# Revit family: Kingsway Stable DA Doorset - S_Flush
name_source: partatom
category: Doors
revit_build: Autodesk Revit 2016 (Build: 20150701_1515(x64)
units: mm (PartAtom-declared; Revit-internal decimal feet)

## family parameters
Always vertical = Yes
Cut with Voids When Loaded = No
Host = Wall
OmniClass Number = 23.30.10.00
OmniClass Title = Doors
Room Calculation Point = No
Shared = No

## types (1)
- 1000 x 2100
    Action = Double (Anti-Barricade)
    Analytic Construction = <None>
    Architrave Finish = <By Category>
    Architrave Material = Solid hardwood.
    Bead Material = None.
    Configuration = Single Leaf (Stable)
    Description = The twin leaf, stable split door double action for clinics or servery areas.
    Door - Leaf Finish Notes = Classic Veneer – 'Oak', 'Ash', or 'Beech'
Classic Laminate – 'Formica Door Collection Matte58 Woods', or 'Formica Collection Colors'
Signature - 'Malmo (Egger H877 ST86 Light Lakeland Acacia)', 'Manhattan (Egger H1734 ST9 Intarsie Walnut Horizontal)', or 'Mayfair (Egger H853 ST86 Lava Grey Fleetwood Horizontal)'
    Door Leaf Height = 2054 mm  [stored 6.73885 ft]
    Door Leaf Width = 849 mm  [stored 2.78543 ft]
    DoorLeafHeightLower = 1000 mm  [stored 3.28084 ft]
    DoorLeafHeightUpper = 1051 mm
    Durability = Severe Duty Mechanical Strength (DD171).
    Error = No
    Fire Rating = NFR / FD30S
    Frame Finish = <By Category>
    Frame Thickness = 32 mm  [stored 0.104987 ft]
    Frame Thickness Leading Edge = 44 mm  [stored 0.144357 ft]
    Function = Interior
    Hardware - Blanking Plate = <By Category>
    Hardware - Door Top Monitor = <By Category>
    Hardware - Eurocylinder Escutcheon = <By Category>
    Hardware - External Override = <By Category>
    Hardware - External Override with Indicator = <By Category>
    Hardware - Hinge = <By Category>
    Hardware - Pull Handle = <By Category>
    Hardware - SwingStop = <By Category>
    Hardware - Thumb Turn = <By Category>
    Height = 2100 mm
    KG202SwingHinge = Yes
    KG206SwingStopAntiBarricadeDoorStop = Yes
    Keynote = L20
    Leaf Core Structure = Flamebreak - Solid timber core comprising three layers of solid hardwood.
    Leaf Height Limits = 2100 mm
    Leaf Swing Radius = 892 mm
    Leaf Width Limits = 1100 mm
    Lipping Finish = <By Category>
    Lipping Material = Exposed 10mm solid hardwood to all four edges.
    Manufacturer = Kingsway Group
    Model = Stable DA Doorset
    Rough Height = 2100 mm
    Rough Width = 1000 mm  [stored 3.28084 ft]
    SwingStop Height = 2061 mm  [stored 6.76181 ft]
    Telephone = 01322 610 470
    Thickness = 44 mm  [stored 0.144357 ft]
    URL = https://www.kingswaygroupglobal.com
    Version = 1.0
    Vision Panel = None.
    Wall Closure = Neither
    Width = 1000 mm  [stored 3.28084 ft]

note: [stored X ft] marks values corroborated as IEEE doubles in the binary element streams (Revit-internal decimal feet)

## geometry (parser evidence)
native form markers: Blend x2, Sweep x48
no freeform markers — native parametric forms only
